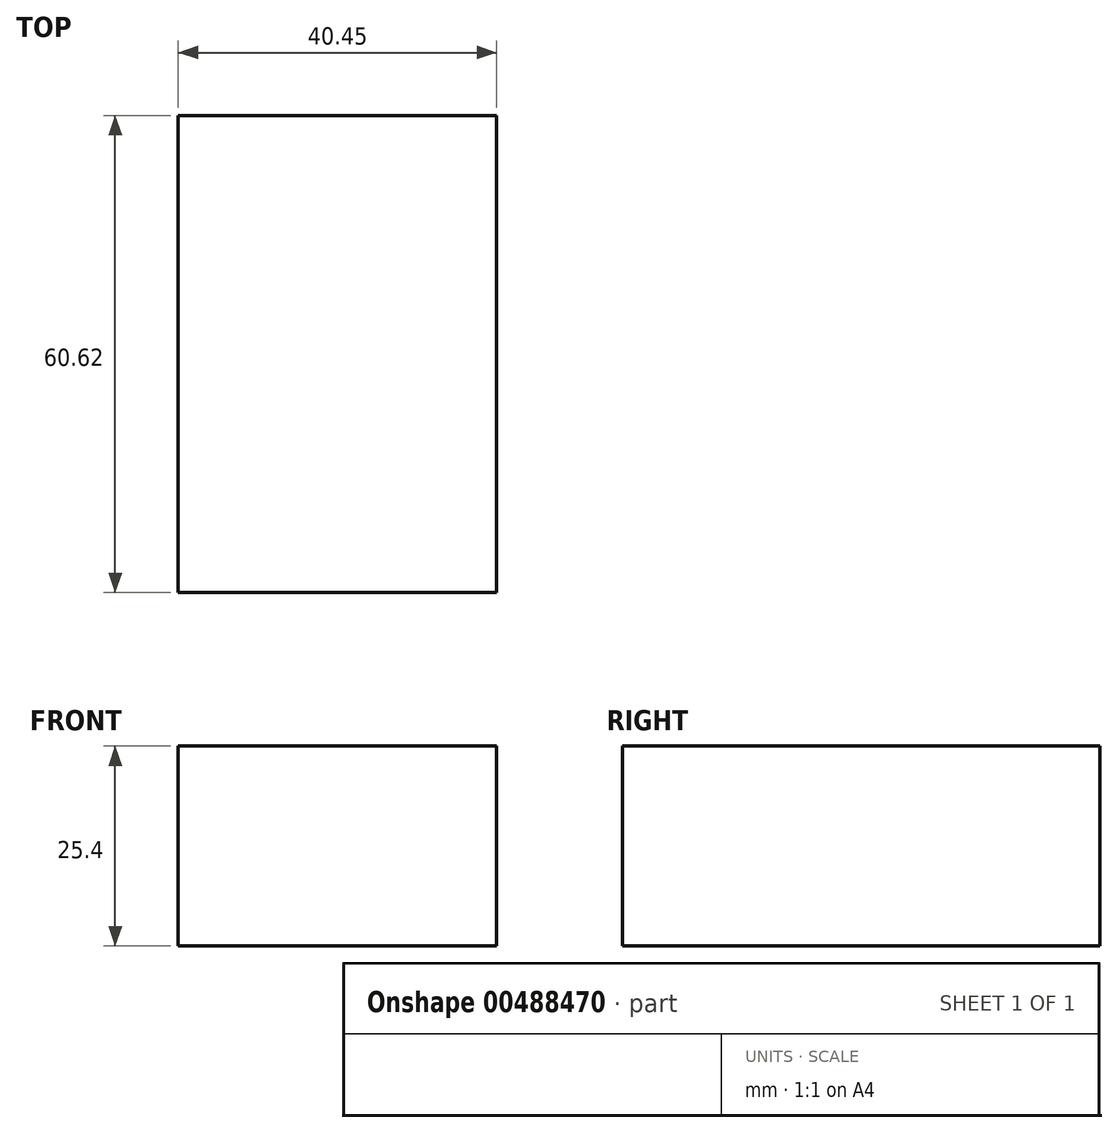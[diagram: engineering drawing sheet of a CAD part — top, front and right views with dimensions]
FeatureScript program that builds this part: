
annotation { "Feature Type Name" : "Feature", "Feature Type Description" : "" }
export const myFeature = defineFeature(function(context is Context, id is Id, definition is map)
    precondition{}
    {
        {
            var Q0;
            Q0=qCreatedBy(makeId("Top.planeOp"),FACE);
            var sketch = newSketch(context, id + "F0", { "sketchPlane" : qUnion([Q0])});
            skLineSegment(sketch, "E0.bottom", {"start": v(44.7, 0) * mm, "end": v(0, 0) * mm});
            skLineSegment(sketch, "E0.top", {"start": v(44.7, 65.12) * mm, "end": v(0, 65.12) * mm});
            skLineSegment(sketch, "E0.left", {"start": v(44.7, 0) * mm, "end": v(44.7, 65.12) * mm});
            skLineSegment(sketch, "E0.right", {"start": v(0, 0) * mm, "end": v(0, 65.12) * mm});
            skLineSegment(sketch, "E1.bottom", {"start": v(-14.29, -117.38) * mm, "end": v(28.4, -117.38) * mm});
            skLineSegment(sketch, "E1.top", {"start": v(-14.29, 32.72) * mm, "end": v(28.4, 32.72) * mm});
            skLineSegment(sketch, "E1.left", {"start": v(-14.29, -117.38) * mm, "end": v(-14.29, 32.72) * mm});
            skLineSegment(sketch, "E1.right", {"start": v(28.4, -117.38) * mm, "end": v(28.4, 32.72) * mm});
            skLineSegment(sketch, "E2.bottom", {"start": v(46.2, -82.49) * mm, "end": v(50.2, -82.49) * mm});
            skLineSegment(sketch, "E2.top", {"start": v(46.2, -63.91) * mm, "end": v(50.2, -63.91) * mm});
            skLineSegment(sketch, "E2.left", {"start": v(46.2, -82.49) * mm, "end": v(46.2, -63.91) * mm});
            skLineSegment(sketch, "E2.right", {"start": v(50.2, -82.49) * mm, "end": v(50.2, -63.91) * mm});
            skLineSegment(sketch, "E3.bottom", {"start": v(90.64, -63.91) * mm, "end": v(50.2, -63.91) * mm});
            skLineSegment(sketch, "E3.top", {"start": v(90.64, -124.53) * mm, "end": v(50.2, -124.53) * mm});
            skLineSegment(sketch, "E3.left", {"start": v(90.64, -63.91) * mm, "end": v(90.64, -124.53) * mm});
            skLineSegment(sketch, "E3.right", {"start": v(50.2, -63.91) * mm, "end": v(50.2, -124.53) * mm});
            skSolve(sketch);
        }
        {
            var Q0;
            {var subQ2=sQuery(id+"F0.wireOp",EDGE,"E3.bottom");Q0=makeQuery(id+"F0.imprint","IMPRINT",FACE,{"disambiguationData":[TD([[makeQuery(id+"F0.imprint","IMPRINT",EDGE,{"derivedFrom":subQ2}),1.0]])]});}
            extrude(context, id + "F1", {"entities" : qUnion([Q0]), "depth" : 25.4 * mm});
        }
    });
